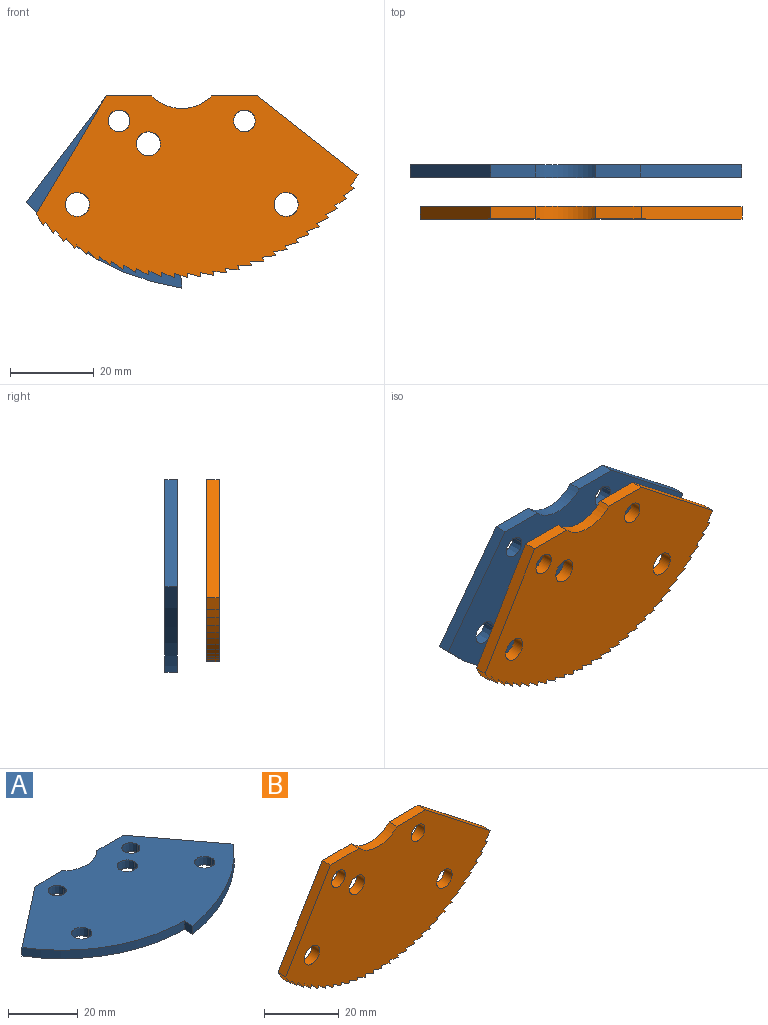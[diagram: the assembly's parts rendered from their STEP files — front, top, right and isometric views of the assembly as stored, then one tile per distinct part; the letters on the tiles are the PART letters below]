
ASSEMBLY  parts=2 mates=1
PART A: 20 faces, bbox 79.5x46x3 mm
  f0: extruded ~5.2x3mm, area 24.5mm2, adj f5,f6,f19
  f1: extruded ~5.8x3mm, area 27.3mm2, adj f5,f6,f18
  f2: extruded ~5.8x3mm, area 27.3mm2, adj f5,f6,f17
  f3: extruded ~5.2x3mm, area 24.5mm2, adj f5,f6,f16
  f4: extruded ~5.8x3mm, area 27.3mm2, adj f5,f6,f15
  f5: plane 79.46x46mm, normal (0,0,1), area 2314.2mm2, adj f0,f1,f2,f3,f4,f7,f8,f9
  f6: plane 79.46x46mm, normal (0,0,-1), area 2314.2mm2, adj f0,f1,f2,f3,f4,f7,f8,f9
  f7: cylinder r=49.5mm len=42.43mm, axis (0,0,-1), area 152.2mm2, adj f5,f6,f8,f14
  f8: plane 3.5x3mm, normal (-1,0.07,0), area 10.5mm2, adj f5,f6,f7,f9
  f9: cylinder r=62.5mm len=37.27mm, axis (0,0,-1), area 130.1mm2, adj f5,f6,f8,f10
  f10: plane 25.57x19.27mm, normal (0.8,0.6,0), area 96.1mm2, adj f5,f6,f9,f11
  f11: plane 10.86x3mm, normal (0,1,0), area 32.6mm2, adj f5,f6,f10,f12
  f12: cylinder r=10mm len=14.28mm, axis (0,0,-1), area 47.7mm2, adj f5,f6,f11,f13
  f13: plane 10.86x3mm, normal (0,1,0), area 32.6mm2, adj f5,f6,f12,f14
  f14: plane 24.19x18.9mm, normal (-0.62,0.79,0), area 92.1mm2, adj f5,f6,f7,f13
  f15: extruded ~5.8x3mm, area 27.3mm2, adj f4,f5,f6
  f16: extruded ~5.2x3mm, area 24.5mm2, adj f3,f5,f6
  f17: extruded ~5.8x3mm, area 27.3mm2, adj f2,f5,f6
  f18: extruded ~5.8x3mm, area 27.3mm2, adj f1,f5,f6
  f19: extruded ~5.2x3mm, area 24.5mm2, adj f0,f5,f6
PART B: 69 faces, bbox 77x3x43.5 mm
  f0: cylinder r=49.5mm len=3mm, axis (0,1,0), area 9.3mm2, adj f4,f6,f7,f63
  f1: cylinder r=10mm len=14.3mm, axis (0,1,0), area 47.8mm2, adj f2,f5,f6,f7
  f2: plane 10.9x3mm, normal (0,0,1), area 32.7mm2, adj f1,f3,f6,f7
  f3: plane 28.22x16.74mm, normal (-0.86,0,0.51), area 98.4mm2, adj f2,f6,f7,f8
  f4: plane 24.16x18.87mm, normal (0.62,0,0.79), area 92mm2, adj f0,f5,f6,f7
  f5: plane 10.9x3mm, normal (0,0,1), area 32.7mm2, adj f1,f4,f6,f7
  f6: plane 77x43.49mm, normal (0,-1,0), area 2251.9mm2, adj f0,f1,f2,f3,f4,f5,f8,f9
  f7: plane 77x43.49mm, normal (0,1,0), area 2251.9mm2, adj f0,f1,f2,f3,f4,f5,f8,f9
  f8: plane 3x2.84mm, normal (-0.87,0,-0.49), area 9.8mm2, adj f3,f6,f7,f9
  f9: plane 3x0.75mm, normal (0.75,0,-0.66), area 3mm2, adj f6,f7,f8,f10
  f10: plane 3x2.74mm, normal (-0.84,0,-0.54), area 9.8mm2, adj f6,f7,f9,f11
  f11: plane 3x0.79mm, normal (0.79,0,-0.61), area 3mm2, adj f6,f7,f10,f12
  f12: plane 3x2.62mm, normal (-0.81,0,-0.59), area 9.8mm2, adj f6,f7,f11,f13
  f13: plane 3x0.83mm, normal (0.83,0,-0.56), area 3mm2, adj f6,f7,f12,f14
  f14: plane 3x2.5mm, normal (-0.77,0,-0.64), area 9.8mm2, adj f6,f7,f13,f15
  f15: plane 3x0.86mm, normal (0.86,0,-0.51), area 3mm2, adj f6,f7,f14,f16
  f16: plane 3x2.37mm, normal (-0.73,0,-0.69), area 9.8mm2, adj f6,f7,f15,f17
  f17: plane 3x0.89mm, normal (0.89,0,-0.45), area 3mm2, adj f6,f7,f16,f18
  f18: plane 3x2.39mm, normal (-0.68,0,-0.73), area 9.8mm2, adj f6,f7,f17,f19
  f19: plane 3x0.92mm, normal (0.92,0,-0.4), area 3mm2, adj f6,f7,f18,f20
  f20: plane 3x2.52mm, normal (-0.63,0,-0.77), area 9.8mm2, adj f6,f7,f19,f21
  f21: plane 3x0.94mm, normal (0.94,0,-0.34), area 3mm2, adj f6,f7,f20,f22
  f22: plane 3x2.64mm, normal (-0.59,0,-0.81), area 9.8mm2, adj f6,f7,f21,f23
  f23: plane 3x0.96mm, normal (0.96,0,-0.28), area 3mm2, adj f6,f7,f22,f24
  f24: plane 3x2.76mm, normal (-0.53,0,-0.85), area 9.8mm2, adj f6,f7,f23,f25
  f25: plane 3x0.98mm, normal (0.98,0,-0.22), area 3mm2, adj f6,f7,f24,f26
  f26: plane 3x2.86mm, normal (-0.48,0,-0.88), area 9.8mm2, adj f6,f7,f25,f27
  f27: plane 3x0.99mm, normal (0.99,0,-0.16), area 3mm2, adj f6,f7,f26,f28
  f28: plane 3x2.95mm, normal (-0.43,0,-0.9), area 9.8mm2, adj f6,f7,f27,f29
  f29: plane 3x1mm, normal (1,0,-0.1), area 3mm2, adj f6,f7,f28,f30
  f30: plane 3.03x3mm, normal (-0.37,0,-0.93), area 9.8mm2, adj f6,f7,f29,f31
  f31: plane 3x1mm, normal (1,0,-0.03), area 3mm2, adj f6,f7,f30,f32
  f32: plane 3.1x3mm, normal (-0.31,0,-0.95), area 9.8mm2, adj f6,f7,f31,f33
  f33: plane 3x1mm, normal (1,0,0.03), area 3mm2, adj f6,f7,f32,f34
  f34: plane 3.16x3mm, normal (-0.25,0,-0.97), area 9.8mm2, adj f6,f7,f33,f35
  f35: plane 3x1mm, normal (1,0,0.09), area 3mm2, adj f6,f7,f34,f36
  f36: plane 3.2x3mm, normal (-0.19,0,-0.98), area 9.8mm2, adj f6,f7,f35,f37
  f37: plane 3x0.99mm, normal (0.99,0,0.15), area 3mm2, adj f6,f7,f36,f38
  f38: plane 3.23x3mm, normal (-0.13,0,-0.99), area 9.8mm2, adj f6,f7,f37,f39
  f39: plane 3x0.98mm, normal (0.98,0,0.21), area 3mm2, adj f6,f7,f38,f40
  f40: plane 3.25x3mm, normal (-0.07,0,-1), area 9.8mm2, adj f6,f7,f39,f41
  f41: plane 3x0.96mm, normal (0.96,0,0.27), area 3mm2, adj f6,f7,f40,f42
  f42: plane 3.26x3mm, normal (-0.01,0,-1), area 9.8mm2, adj f6,f7,f41,f43
  f43: plane 3x0.94mm, normal (0.94,0,0.33), area 3mm2, adj f6,f7,f42,f44
  f44: plane 3.25x3mm, normal (0.06,0,-1), area 9.8mm2, adj f6,f7,f43,f45
  f45: plane 3x0.92mm, normal (0.92,0,0.39), area 3mm2, adj f6,f7,f44,f46
  f46: plane 3.24x3mm, normal (0.12,0,-0.99), area 9.8mm2, adj f6,f7,f45,f47
  f47: plane 3x0.9mm, normal (0.9,0,0.45), area 3mm2, adj f6,f7,f46,f48
  f48: plane 3.21x3mm, normal (0.18,0,-0.98), area 9.8mm2, adj f6,f7,f47,f49
  f49: plane 3x0.87mm, normal (0.87,0,0.5), area 3mm2, adj f6,f7,f48,f50
  f50: plane 3.16x3mm, normal (0.24,0,-0.97), area 9.8mm2, adj f6,f7,f49,f51
  f51: plane 3x0.83mm, normal (0.83,0,0.55), area 3mm2, adj f6,f7,f50,f52
  f52: plane 3.11x3mm, normal (0.3,0,-0.95), area 9.8mm2, adj f6,f7,f51,f53
  f53: plane 3x0.8mm, normal (0.8,0,0.6), area 3mm2, adj f6,f7,f52,f54
  f54: plane 3.04x3mm, normal (0.36,0,-0.93), area 9.8mm2, adj f6,f7,f53,f55
  f55: plane 3x0.76mm, normal (0.76,0,0.65), area 3mm2, adj f6,f7,f54,f56
  f56: plane 3x2.96mm, normal (0.42,0,-0.91), area 9.8mm2, adj f6,f7,f55,f57
  f57: plane 3x0.72mm, normal (0.72,0,0.7), area 3mm2, adj f6,f7,f56,f58
  f58: plane 3x2.87mm, normal (0.47,0,-0.88), area 9.8mm2, adj f6,f7,f57,f59
  f59: plane 3x0.74mm, normal (0.67,0,0.74), area 3mm2, adj f6,f7,f58,f60
  f60: plane 3x2.77mm, normal (0.53,0,-0.85), area 9.8mm2, adj f6,f7,f59,f61
  f61: plane 3x0.78mm, normal (0.62,0,0.78), area 3mm2, adj f6,f7,f60,f62
  f62: plane 3x2.66mm, normal (0.58,0,-0.82), area 9.8mm2, adj f6,f7,f61,f63
  f63: plane 3x0.82mm, normal (0.58,0,0.82), area 3mm2, adj f0,f6,f7,f62
  f64: cylinder r=2.9mm len=5.8mm, axis (0,1,0), area 54.7mm2, adj f6,f7
  f65: cylinder r=2.6mm len=5.2mm, axis (0,1,0), area 49mm2, adj f6,f7
  f66: cylinder r=2.9mm len=5.8mm, axis (0,1,0), area 54.7mm2, adj f6,f7
  f67: cylinder r=2.9mm len=5.8mm, axis (0,1,0), area 54.7mm2, adj f6,f7
  f68: cylinder r=2.6mm len=5.2mm, axis (0,1,0), area 49mm2, adj f6,f7
PLACE A rot(axis=(0,0.71,0.71),180deg) t=(0,-169,0)mm
PLACE B at identity fixed
MATE fastened B.f1 <-> A.f12  axis (0,-1,0) through (0,-3,0)mm
